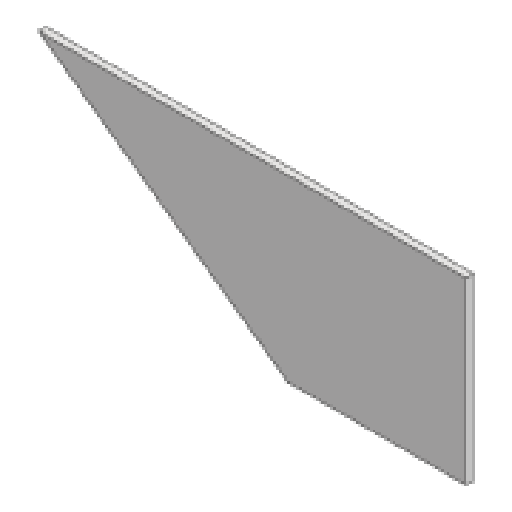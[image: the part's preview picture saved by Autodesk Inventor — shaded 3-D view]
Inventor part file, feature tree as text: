
AUTODESK INVENTOR PART (.ipt)
format: ipt  version: 2025 (Build 290162000, 162)  size: 97,280 bytes
history: native  units: mm
features: other x6, reference x4, extrude x1, sketch x1
ambient origin geometry x8: Origin, YZ Plane, XZ Plane, XY Plane, X Axis, Y Axis, Z Axis, Center Point
bodies: Solid1 (feature_tree)
feature tree (12):
  extrude  "Extrusion1"  [1 undecoded]
  sketch  "Sketch1"  dims[d0=5.0mm d1=0.0mm]
  reference  "Reference1"
  reference  "Reference2"
  reference  "Reference3"
  reference  "Reference4"
  other  "<userpath>\Desktop\puppycat\woodhouseMK1.iam"
  other  "woodhouseMK1.iam"
  other  "trackBase:1"
  other  "6pt9inStrut:1"
  other  "lowerSkidPlateRear:1"
  other  "upperFrontSkidPlate:1"
note: 1 required parameter value undecoded (feature->parameter linkage not recoverable at this tier; creation-order binding heuristic only, values carry confidence <= 0.55)
